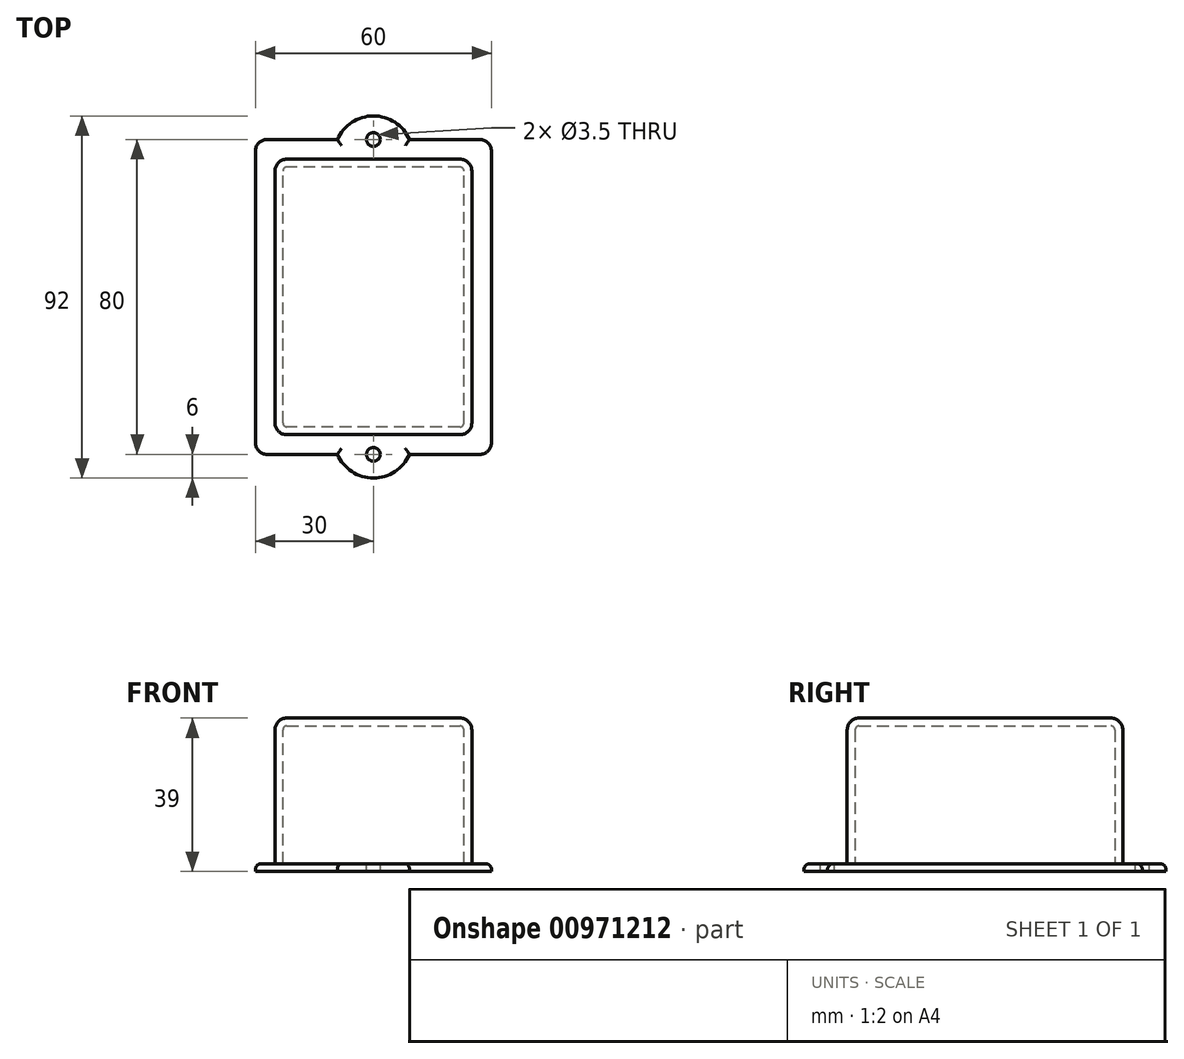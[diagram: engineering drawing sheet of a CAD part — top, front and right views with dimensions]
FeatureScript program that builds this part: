
annotation { "Feature Type Name" : "Feature", "Feature Type Description" : "" }
export const myFeature = defineFeature(function(context is Context, id is Id, definition is map)
    precondition{}
    {
        {
            var Q0;
            Q0=qCreatedBy(makeId("Top.planeOp"),FACE);
            var sketch = newSketch(context, id + "F0", { "sketchPlane" : qUnion([Q0])});
            skLineSegment(sketch, "E0.bottom", {"start": v(25, -35) * mm, "end": v(-25, -35) * mm});
            skLineSegment(sketch, "E0.top", {"start": v(25, 35) * mm, "end": v(-25, 35) * mm});
            skLineSegment(sketch, "E0.left", {"start": v(25, -35) * mm, "end": v(25, 35) * mm});
            skLineSegment(sketch, "E0.right", {"start": v(-25, -35) * mm, "end": v(-25, 35) * mm});
            skPoint(sketch, "E0.middle", {"position": v(0, 0) * mm});
            skSolve(sketch);
        }
        {
            var Q0;
            Q0=makeQuery(id+"F0.imprint","IMPRINT",FACE,{"disambiguationData":[TD([[makeQuery(id+"F0.imprint","IMPRINT",EDGE,{"derivedFrom":sQuery(id+"F0.wireOp",EDGE,"E0.bottom")}),-1.0]])]});
            extrude(context, id + "F1", {"entities" : qUnion([Q0]), "depth" : 37 * mm, "offsetDistance" : 25 * mm});
        }
        {
            var Q0;
            Q0=makeQuery(id+"F1.opExtrude","CAP_EDGE",EDGE,{"disambiguationData":[OSD([sQuery(id+"F0.wireOp",EDGE,"E0.left")])],"isStart":false});
            var Q1;
            Q1=makeQuery(id+"F1.opExtrude","CAP_EDGE",EDGE,{"disambiguationData":[OSD([sQuery(id+"F0.wireOp",EDGE,"E0.bottom")])],"isStart":false});
            var Q2;
            Q2=makeQuery(id+"F1.opExtrude","SWEPT_EDGE",EDGE,{"disambiguationData":[OSD([sQuery(id+"F0.wireOp",EDGE,"E0.bottom"),sQuery(id+"F0.wireOp",EDGE,"E0.left")])]});
            var Q3;
            Q3=makeQuery(id+"F1.opExtrude","SWEPT_EDGE",EDGE,{"disambiguationData":[OSD([sQuery(id+"F0.wireOp",EDGE,"E0.top"),sQuery(id+"F0.wireOp",EDGE,"E0.left")])]});
            var Q4;
            Q4=makeQuery(id+"F1.opExtrude","CAP_EDGE",EDGE,{"disambiguationData":[OSD([sQuery(id+"F0.wireOp",EDGE,"E0.top")])],"isStart":false});
            var Q5;
            Q5=makeQuery(id+"F1.opExtrude","CAP_EDGE",EDGE,{"disambiguationData":[OSD([sQuery(id+"F0.wireOp",EDGE,"E0.right")])],"isStart":false});
            var Q6;
            Q6=makeQuery(id+"F1.opExtrude","SWEPT_EDGE",EDGE,{"disambiguationData":[OSD([sQuery(id+"F0.wireOp",EDGE,"E0.bottom"),sQuery(id+"F0.wireOp",EDGE,"E0.right")])]});
            var Q7;
            Q7=makeQuery(id+"F1.opExtrude","SWEPT_EDGE",EDGE,{"disambiguationData":[OSD([sQuery(id+"F0.wireOp",EDGE,"E0.top"),sQuery(id+"F0.wireOp",EDGE,"E0.right")])]});
            fillet(context, id + "F2", {"entities" : qUnion([Q0, Q1, Q2, Q3, Q4, Q5, Q6, Q7]), "tangentPropagation" : true, "radius" : 3 * mm, "defaultsChanged" : true, "vertexSettings" : [], "allowEdgeOverflow" : false});
        }
        {
            var Q0;
            Q0=makeQuery(id+"F1.opExtrude","CAP_FACE",FACE,{"disambiguationData":[OSD([sQuery(id+"F0.wireOp",EDGE,"E0.bottom"),sQuery(id+"F0.wireOp",EDGE,"E0.top"),sQuery(id+"F0.wireOp",EDGE,"E0.left"),sQuery(id+"F0.wireOp",EDGE,"E0.right")])],"isStart":true});
            shell(context, id + "F3", {"entities" : qUnion([Q0]), "thickness" : 2 * mm});
        }
        {
            var Q0;
            Q0=qCreatedBy(makeId("Top.planeOp"),FACE);
            var sketch = newSketch(context, id + "F4", { "sketchPlane" : qUnion([Q0])});
            skLineSegment(sketch, "E1.0", {"start": v(27, -40) * mm, "end": v(9.17, -40) * mm});
            skArc(sketch, "E1.1", {"start": v(30, -37) * mm, "mid": v(29.12, -39.12) * mm, "end": v(27, -40) * mm});
            skArc(sketch, "E1.2", {"start": v(-27, -40) * mm, "mid": v(-29.12, -39.12) * mm, "end": v(-30, -37) * mm});
            skLineSegment(sketch, "E1.3", {"start": v(30, -37) * mm, "end": v(30, 37) * mm});
            skLineSegment(sketch, "E1.4", {"start": v(-30, -37) * mm, "end": v(-30, 37) * mm});
            skArc(sketch, "E1.5", {"start": v(-30, 37) * mm, "mid": v(-29.12, 39.12) * mm, "end": v(-27, 40) * mm});
            skLineSegment(sketch, "E1.6", {"start": v(27, 40) * mm, "end": v(9.17, 40) * mm});
            skArc(sketch, "E1.7", {"start": v(27, 40) * mm, "mid": v(29.12, 39.12) * mm, "end": v(30, 37) * mm});
            skArc(sketch, "E2", {"start": v(-9.17, -40) * mm, "mid": v(0, -46) * mm, "end": v(9.17, -40) * mm});
            skArc(sketch, "E3.MirrorC", {"start": v(-9.17, 40) * mm, "mid": v(0, 46) * mm, "end": v(9.17, 40) * mm});
            skPoint(sketch, "E4", {"position": v(30, 0) * mm});
            skPoint(sketch, "E5", {"position": v(-30, 0) * mm});
            skPoint(sketch, "E6", {"position": v(0, -40) * mm});
            skPoint(sketch, "E7", {"position": v(0, 40) * mm});
            skLineSegment(sketch, "E8.trimOffspring", {"start": v(-9.17, 40) * mm, "end": v(-27, 40) * mm});
            skLineSegment(sketch, "E9.trimOffspring", {"start": v(-9.17, -40) * mm, "end": v(-27, -40) * mm});
            skLineSegment(sketch, "E10", {"start": v(-47.05, -37) * mm, "end": v(34.58, -37) * mm, "construction": true});
            skLineSegment(sketch, "E11", {"start": v(40.17, 37) * mm, "end": v(-44.52, 37) * mm, "construction": true});
            skLineSegment(sketch, "E12", {"start": v(-27, -48.1) * mm, "end": v(-27, 47.4) * mm, "construction": true});
            skLineSegment(sketch, "E13", {"start": v(27, -49.75) * mm, "end": v(27, 48.81) * mm, "construction": true});
            skCircle(sketch, "E14", {"center": v(0, -40) * mm, "radius": 1.75 * mm});
            skCircle(sketch, "E15", {"center": v(0, 40) * mm, "radius": 1.75 * mm});
            skSolve(sketch);
        }
        {
            var Q0;
            Q0=makeQuery(id+"F4.imprint","IMPRINT",FACE,{"disambiguationData":[TD([[makeQuery(id+"F4.imprint","IMPRINT",EDGE,{"derivedFrom":sQuery(id+"F4.wireOp",EDGE,"9LFbx52S-rh09-otIV-B73i-fFjCxGltCRpn")}),-1.0]])]});
            var Q1;
            {var subQ0=sQuery(id+"F4.wireOp",EDGE,"c23e8a2d-9faa-4340-a5da-aeb760b3d1e30.MirrorCS");var subQ1=sQuery(id+"F4.wireOp",EDGE,"E1.0");var subQ2=makeQuery(id+"F4.imprint","INTERSECT",VERTEX,{"derivedFrom":[subQ1,subQ0]});Q1=makeQuery(id+"F4.imprint","IMPRINT",FACE,{"disambiguationData":[TD([[makeQuery(id+"F4.imprint","IMPRINT",EDGE,{"disambiguationData":[TD([[subQ2,-1.0]])],"derivedFrom":subQ1}),1.0]])]});}
            var Q2;
            Q2=makeQuery(id+"F4.imprint","IMPRINT",FACE,{"disambiguationData":[TD([[makeQuery(id+"F4.imprint","IMPRINT",EDGE,{"derivedFrom":sQuery(id+"F4.wireOp",EDGE,"b936bb06-83af-488a-af87-56cb3f7d742f.0")}),1.0]])]});
            var Q3;
            Q3=makeQuery(id+"F4.imprint","IMPRINT",FACE,{"disambiguationData":[TD([[makeQuery(id+"F4.imprint","IMPRINT",EDGE,{"derivedFrom":sQuery(id+"F4.wireOp",EDGE,"b936bb06-83af-488a-af87-56cb3f7d742f.0")}),-1.0]])]});
            var Q4;
            {var subQ0=sQuery(id+"F4.wireOp",EDGE,"a43832f9-bdfb-4a58-aca9-dc167431100e0.MirrorCS");var subQ1=sQuery(id+"F4.wireOp",EDGE,"E1.6");var subQ2=makeQuery(id+"F4.imprint","INTERSECT",VERTEX,{"derivedFrom":[subQ1,subQ0]});Q4=makeQuery(id+"F4.imprint","IMPRINT",FACE,{"disambiguationData":[TD([[makeQuery(id+"F4.imprint","IMPRINT",EDGE,{"disambiguationData":[TD([[subQ2,-1.0]])],"derivedFrom":subQ1}),-1.0]])]});}
            var Q5;
            Q5=makeQuery(id+"F4.imprint","IMPRINT",FACE,{"disambiguationData":[TD([[makeQuery(id+"F4.imprint","IMPRINT",EDGE,{"derivedFrom":sQuery(id+"F4.wireOp",EDGE,"c486c68a-be01-4998-a10b-fb3b4db6286b0.MirrorC")}),1.0]])]});
            var Q6;
            {var subQ0=sQuery(id+"F4.wireOp",EDGE,"E2");var subQ1=sQuery(id+"F4.wireOp",EDGE,"E1.0");var subQ2=makeQuery(id+"F4.imprint","INTERSECT",VERTEX,{"disambiguationData":[OD(0.0)],"derivedFrom":[subQ1,subQ0]});Q6=makeQuery(id+"F4.imprint","IMPRINT",FACE,{"disambiguationData":[TD([[makeQuery(id+"F4.imprint","IMPRINT",EDGE,{"disambiguationData":[TD([[subQ2,-1.0]])],"derivedFrom":subQ1}),1.0]])]});}
            var Q7;
            {var subQ0=sQuery(id+"F4.wireOp",EDGE,"E2");var subQ1=sQuery(id+"F4.wireOp",EDGE,"E1.0");var subQ2=makeQuery(id+"F4.imprint","INTERSECT",VERTEX,{"disambiguationData":[OD(0.0)],"derivedFrom":[subQ1,subQ0]});Q7=makeQuery(id+"F4.imprint","IMPRINT",FACE,{"disambiguationData":[TD([[makeQuery(id+"F4.imprint","IMPRINT",EDGE,{"disambiguationData":[TD([[subQ2,1.0]])],"derivedFrom":subQ1}),-1.0]])]});}
            var Q8;
            {var subQ0=sQuery(id+"F4.wireOp",EDGE,"E3.MirrorC");var subQ1=sQuery(id+"F4.wireOp",EDGE,"E1.6");var subQ2=makeQuery(id+"F4.imprint","INTERSECT",VERTEX,{"disambiguationData":[OD(0.0)],"derivedFrom":[subQ1,subQ0]});Q8=makeQuery(id+"F4.imprint","IMPRINT",FACE,{"disambiguationData":[TD([[makeQuery(id+"F4.imprint","IMPRINT",EDGE,{"disambiguationData":[TD([[subQ2,-1.0]])],"derivedFrom":subQ1}),-1.0]])]});}
            var Q9;
            {var subQ0=sQuery(id+"F4.wireOp",EDGE,"E3.MirrorC");var subQ1=sQuery(id+"F4.wireOp",EDGE,"E1.6");var subQ2=makeQuery(id+"F4.imprint","INTERSECT",VERTEX,{"disambiguationData":[OD(0.0)],"derivedFrom":[subQ1,subQ0]});Q9=makeQuery(id+"F4.imprint","IMPRINT",FACE,{"disambiguationData":[TD([[makeQuery(id+"F4.imprint","IMPRINT",EDGE,{"disambiguationData":[TD([[subQ2,1.0]])],"derivedFrom":subQ1}),1.0]])]});}
            var Q10;
            {var subQ0=sQuery(id+"F4.wireOp",EDGE,"E2");var subQ1=sQuery(id+"F4.wireOp",EDGE,"E1.0");var subQ2=makeQuery(id+"F4.imprint","INTERSECT",VERTEX,{"disambiguationData":[OD(0.0)],"derivedFrom":[subQ1,subQ0]});Q10=makeQuery(id+"F4.imprint","IMPRINT",FACE,{"disambiguationData":[TD([[makeQuery(id+"F4.imprint","IMPRINT",EDGE,{"disambiguationData":[TD([[subQ2,-1.0]])],"derivedFrom":subQ1}),-1.0]])]});}
            var Q11;
            {var subQ0=sQuery(id+"F4.wireOp",EDGE,"E3.MirrorC");var subQ1=sQuery(id+"F4.wireOp",EDGE,"E1.6");var subQ2=makeQuery(id+"F4.imprint","INTERSECT",VERTEX,{"disambiguationData":[OD(0.0)],"derivedFrom":[subQ1,subQ0]});Q11=makeQuery(id+"F4.imprint","IMPRINT",FACE,{"disambiguationData":[TD([[makeQuery(id+"F4.imprint","IMPRINT",EDGE,{"disambiguationData":[TD([[subQ2,-1.0]])],"derivedFrom":subQ1}),1.0]])]});}
            var Q12;
            {var subQ0=sQuery(id+"F4.wireOp",EDGE,"3a6c7b9b-7085-4f0a-a8c1-2304cddefe9f0.MirrorCS");Q12=makeQuery(id+"F4.imprint","IMPRINT",FACE,{"disambiguationData":[TD([[makeQuery(id+"F4.imprint","IMPRINT",EDGE,{"derivedFrom":subQ0}),1.0]])]});}
            var Q13;
            {var subQ0=sQuery(id+"F4.wireOp",EDGE,"UuzkrU5x-ZZf3-1fiV-ERWb-HPsnwtJuWUzC");Q13=makeQuery(id+"F4.imprint","IMPRINT",FACE,{"disambiguationData":[TD([[makeQuery(id+"F4.imprint","IMPRINT",EDGE,{"derivedFrom":subQ0}),-1.0]])]});}
            extrude(context, id + "F5", {"entities" : qUnion([Q0, Q1, Q2, Q3, Q4, Q5, Q6, Q7, Q8, Q9, Q10, Q11, Q12, Q13]), "oppositeDirection" : true, "depth" : 2 * mm, "offsetDistance" : 25 * mm});
        }
        {
            var Q0;
            Q0=makeQuery(id+"F5.opExtrude","CAP_EDGE",EDGE,{"disambiguationData":[OSD([sQuery(id+"F4.wireOp",EDGE,"E1.4")])],"isStart":true});
            var Q1;
            Q1=makeQuery(id+"F5.opExtrude","CAP_EDGE",EDGE,{"disambiguationData":[OSD([sQuery(id+"F4.wireOp",EDGE,"3a6c7b9b-7085-4f0a-a8c1-2304cddefe9f0.MirrorCS")])],"isStart":true});
            var Q2;
            Q2=makeQuery(id+"F5.opExtrude","CAP_EDGE",EDGE,{"disambiguationData":[OSD([sQuery(id+"F4.wireOp",EDGE,"E3.MirrorC")])],"isStart":true});
            var Q3;
            Q3=makeQuery(id+"F5.opExtrude","CAP_EDGE",EDGE,{"disambiguationData":[OSD([sQuery(id+"F4.wireOp",EDGE,"a43832f9-bdfb-4a58-aca9-dc167431100e0.MirrorCS")])],"isStart":true});
            var Q4;
            {var subQ0=sQuery(id+"F4.wireOp",EDGE,"E1.6");Q4=makeQuery(id+"F5.opExtrude","CAP_EDGE",EDGE,{"disambiguationData":[OSD([subQ0]),TDD([makeQuery(id+"F4.imprint","IMPRINT",EDGE,{"disambiguationData":[TD([[makeQuery(id+"F4.imprint","INTERSECT",VERTEX,{"derivedFrom":[subQ0,sQuery(id+"F4.wireOp",EDGE,"E1.7")]}),-1.0]])],"derivedFrom":subQ0})])],"isStart":true});}
            var Q5;
            Q5=makeQuery(id+"F5.opExtrude","CAP_EDGE",EDGE,{"disambiguationData":[OSD([sQuery(id+"F4.wireOp",EDGE,"E1.7")])],"isStart":true});
            var Q6;
            Q6=makeQuery(id+"F5.opExtrude","CAP_EDGE",EDGE,{"disambiguationData":[OSD([sQuery(id+"F4.wireOp",EDGE,"c23e8a2d-9faa-4340-a5da-aeb760b3d1e30.MirrorCS")])],"isStart":true});
            var Q7;
            Q7=makeQuery(id+"F5.opExtrude","CAP_EDGE",EDGE,{"disambiguationData":[OSD([sQuery(id+"F4.wireOp",EDGE,"E2")])],"isStart":true});
            var Q8;
            {var subQ0=sQuery(id+"F4.wireOp",EDGE,"E1.0");Q8=makeQuery(id+"F5.opExtrude","CAP_EDGE",EDGE,{"disambiguationData":[OSD([subQ0]),TDD([makeQuery(id+"F4.imprint","IMPRINT",EDGE,{"disambiguationData":[TD([[makeQuery(id+"F4.imprint","INTERSECT",VERTEX,{"derivedFrom":[subQ0,sQuery(id+"F4.wireOp",EDGE,"UuzkrU5x-ZZf3-1fiV-ERWb-HPsnwtJuWUzC")]}),-1.0]])],"derivedFrom":subQ0})])],"isStart":true});}
            var Q9;
            Q9=makeQuery(id+"F5.opExtrude","CAP_EDGE",EDGE,{"disambiguationData":[OSD([sQuery(id+"F4.wireOp",EDGE,"UuzkrU5x-ZZf3-1fiV-ERWb-HPsnwtJuWUzC")])],"isStart":true});
            fillet(context, id + "F6", {"entities" : qUnion([Q0, Q1, Q2, Q3, Q4, Q5, Q6, Q7, Q8, Q9]), "tangentPropagation" : true, "radius" : 1.5 * mm, "defaultsChanged" : true, "vertexSettings" : [], "allowEdgeOverflow" : false});
        }
    });
